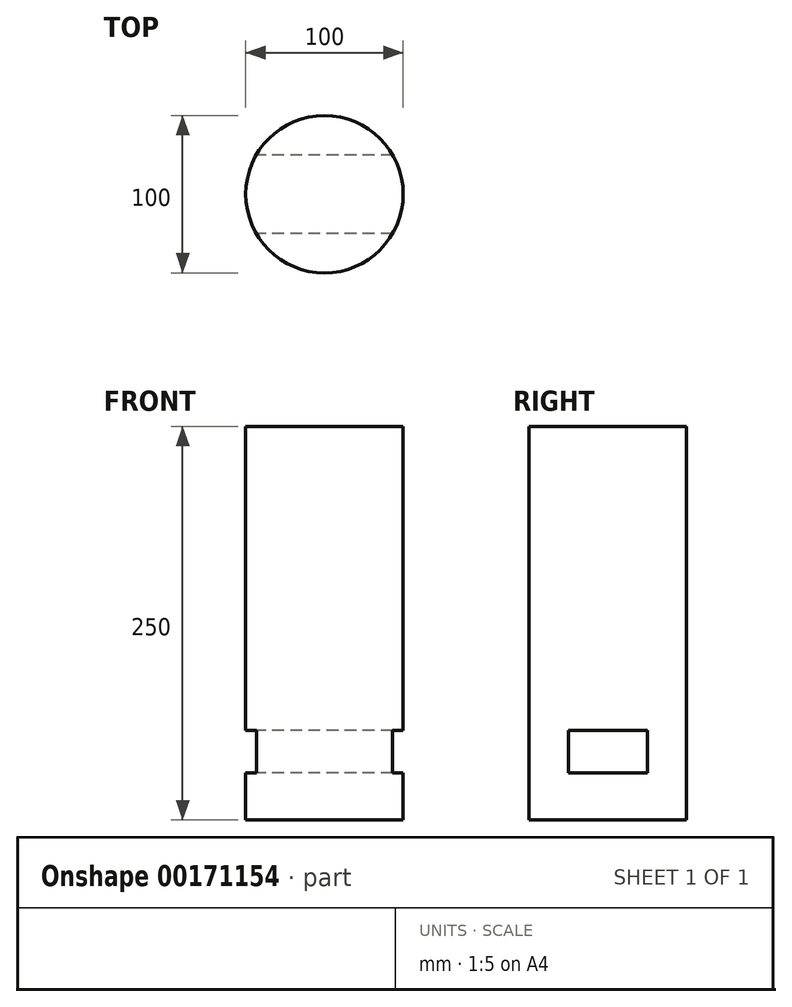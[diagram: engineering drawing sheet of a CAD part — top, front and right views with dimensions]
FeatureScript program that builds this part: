
annotation { "Feature Type Name" : "Feature", "Feature Type Description" : "" }
export const myFeature = defineFeature(function(context is Context, id is Id, definition is map)
    precondition{}
    {
        {
            var Q0;
            Q0=qCreatedBy(makeId("Top.planeOp"),FACE);
            var sketch = newSketch(context, id + "F0", { "sketchPlane" : qUnion([Q0])});
            skCircle(sketch, "E0", {"center": v(0, 0) * mm, "radius": 50 * mm});
            skSolve(sketch);
        }
        {
            var Q0;
            Q0 = qSketchRegion(id + "F0", true);
            extrude(context, id + "F1", {"entities" : qUnion([Q0]), "depth" : 250 * mm});
        }
        {
            var Q0;
            Q0=qCreatedBy(makeId("Right.planeOp"),FACE);
            var sketch = newSketch(context, id + "F2", { "sketchPlane" : qUnion([Q0])});
            skLineSegment(sketch, "E1.bottom", {"start": v(-25, 56.76) * mm, "end": v(25, 56.76) * mm});
            skLineSegment(sketch, "E1.top", {"start": v(-25, 30) * mm, "end": v(25, 30) * mm});
            skLineSegment(sketch, "E1.left", {"start": v(-25, 56.76) * mm, "end": v(-25, 30) * mm});
            skLineSegment(sketch, "E1.right", {"start": v(25, 56.76) * mm, "end": v(25, 30) * mm});
            skSolve(sketch);
        }
        {
            var Q0;
            Q0 = qSketchRegion(id + "F2", true);
            extrude(context, id + "F3", {"entities" : qUnion([Q0]), "operationType" : NewBodyOperationType.REMOVE, "endBound" : BoundingType.UP_TO_NEXT, "depth" : 25 * mm, "hasSecondDirection" : true, "secondDirectionBound" : SecondDirectionBoundingType.UP_TO_NEXT, "secondDirectionOppositeDirection" : true, "secondDirectionDepth" : 25 * mm});
        }
    });
